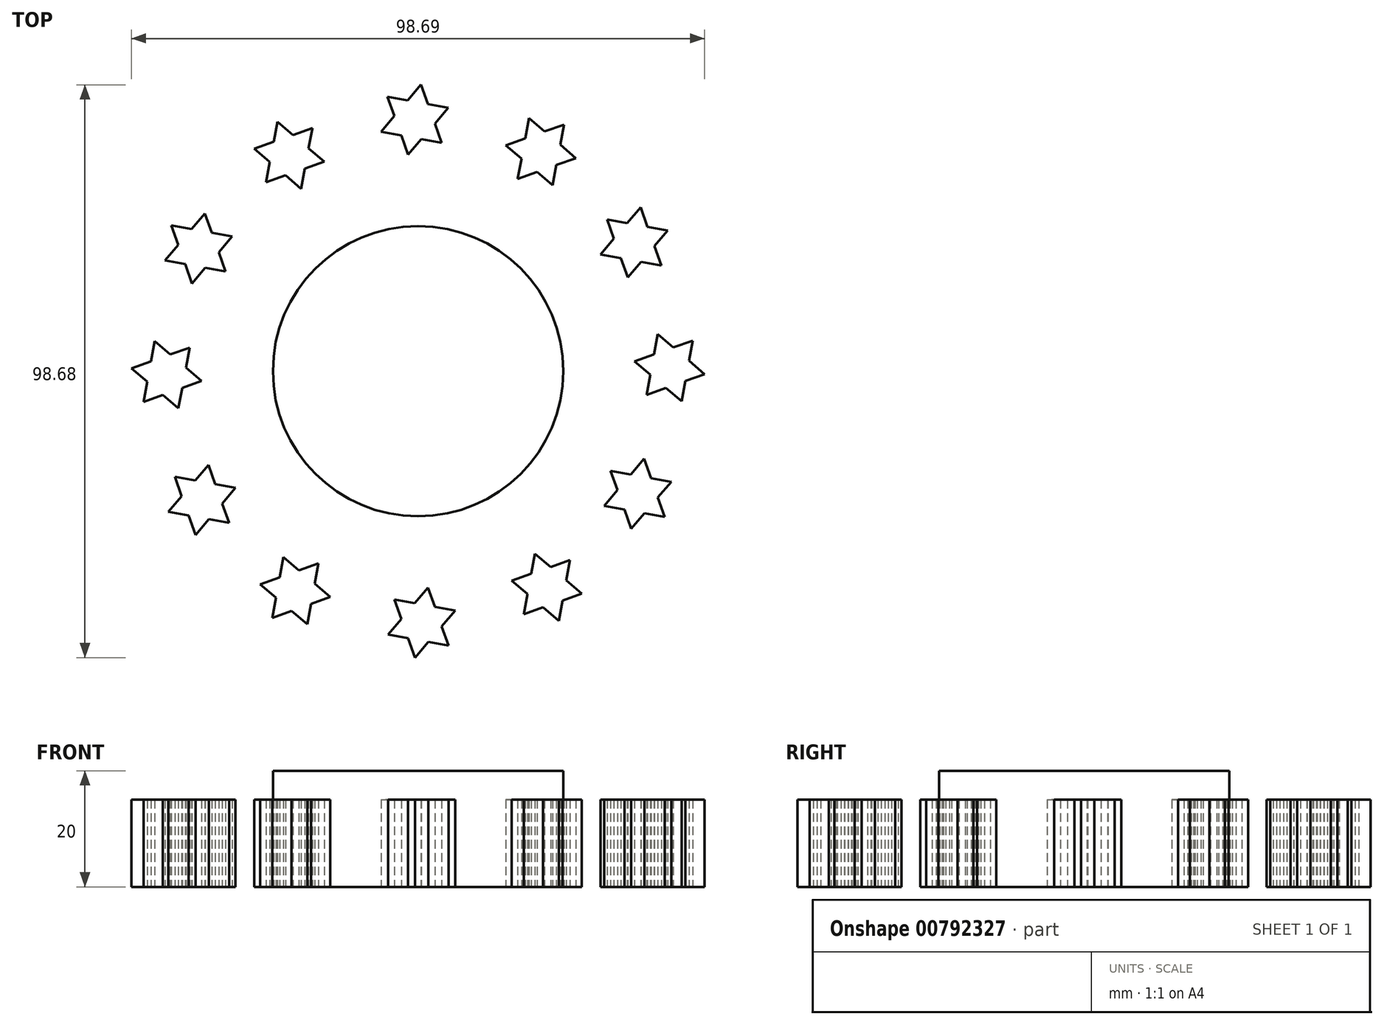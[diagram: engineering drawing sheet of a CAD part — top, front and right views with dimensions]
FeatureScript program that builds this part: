
annotation { "Feature Type Name" : "Feature", "Feature Type Description" : "" }
export const myFeature = defineFeature(function(context is Context, id is Id, definition is map)
    precondition{}
    {
        {
            var Q0;
            Q0=qCreatedBy(makeId("Top.planeOp"),FACE);
            var sketch = newSketch(context, id + "F0", { "sketchPlane" : qUnion([Q0])});
            skCircle(sketch, "E0", {"center": v(0.6, 0) * mm, "radius": 25 * mm});
            skLineSegment(sketch, "E1.0", {"start": v(-1.1, 37.28) * mm, "end": v(-5.78, 41.26) * mm});
            skLineSegment(sketch, "E1.1", {"start": v(-5.78, 41.26) * mm, "end": v(-4.67, 47.29) * mm});
            skLineSegment(sketch, "E1.2", {"start": v(-4.67, 47.29) * mm, "end": v(1.1, 49.34) * mm});
            skLineSegment(sketch, "E1.3", {"start": v(1.1, 49.34) * mm, "end": v(5.78, 45.37) * mm});
            skLineSegment(sketch, "E1.4", {"start": v(5.78, 45.37) * mm, "end": v(4.67, 39.34) * mm});
            skLineSegment(sketch, "E1.5", {"start": v(4.67, 39.34) * mm, "end": v(-1.1, 37.28) * mm});
            skPoint(sketch, "E1.0.midPoint", {"position": v(-3.44, 39.27) * mm});
            skLineSegment(sketch, "E2", {"start": v(-4.67, 47.29) * mm, "end": v(-1.1, 37.28) * mm});
            skLineSegment(sketch, "E3", {"start": v(-4.67, 47.29) * mm, "end": v(5.78, 45.37) * mm});
            skLineSegment(sketch, "E4", {"start": v(-5.78, 41.26) * mm, "end": v(4.67, 39.34) * mm});
            skLineSegment(sketch, "E5", {"start": v(1.1, 49.34) * mm, "end": v(4.67, 39.34) * mm});
            skLineSegment(sketch, "E6", {"start": v(1.1, 49.34) * mm, "end": v(-5.78, 41.26) * mm});
            skLineSegment(sketch, "E7", {"start": v(-1.1, 37.28) * mm, "end": v(5.78, 45.37) * mm});
            skPoint(sketch, "E8.center.orphan", {"position": v(0, 43.31) * mm});
            skSolve(sketch);
        }
        {
            var Q0;
            Q0=makeQuery(id+"F0.imprint","IMPRINT",FACE,{"disambiguationData":[TD([[makeQuery(id+"F0.imprint","IMPRINT",EDGE,{"derivedFrom":sQuery(id+"F0.wireOp",EDGE,"E0")}),1.0]])]});
            extrude(context, id + "F1", {"entities" : qUnion([Q0]), "depth" : 20 * mm, "offsetDistance" : 25 * mm});
        }
        {
            var Q0;
            {var subQ1=sQuery(id+"F0.wireOp",EDGE,"E4");var subQ3=sQuery(id+"F0.wireOp",EDGE,"E7");var subQ4=makeQuery(id+"F0.imprint","INTERSECT",VERTEX,{"derivedFrom":[subQ1,subQ3]});Q0=makeQuery(id+"F0.imprint","IMPRINT",FACE,{"disambiguationData":[TD([[makeQuery(id+"F0.imprint","IMPRINT",EDGE,{"disambiguationData":[TD([[subQ4,-1.0]])],"derivedFrom":subQ3}),-1.0]])]});}
            var Q1;
            {var subQ0=sQuery(id+"F0.wireOp",EDGE,"E6");var subQ1=sQuery(id+"F0.wireOp",EDGE,"E2");var subQ2=makeQuery(id+"F0.imprint","INTERSECT",VERTEX,{"derivedFrom":[subQ1,subQ0]});Q1=makeQuery(id+"F0.imprint","IMPRINT",FACE,{"disambiguationData":[TD([[makeQuery(id+"F0.imprint","IMPRINT",EDGE,{"disambiguationData":[TD([[subQ2,-1.0]])],"derivedFrom":subQ1}),-1.0]])]});}
            var Q2;
            {var subQ1=sQuery(id+"F0.wireOp",EDGE,"E2");var subQ3=sQuery(id+"F0.wireOp",EDGE,"E4");var subQ4=makeQuery(id+"F0.imprint","INTERSECT",VERTEX,{"derivedFrom":[subQ1,subQ3]});Q2=makeQuery(id+"F0.imprint","IMPRINT",FACE,{"disambiguationData":[TD([[makeQuery(id+"F0.imprint","IMPRINT",EDGE,{"disambiguationData":[TD([[subQ4,-1.0]])],"derivedFrom":subQ3}),-1.0]])]});}
            var Q3;
            {var subQ1=sQuery(id+"F0.wireOp",EDGE,"E3");var subQ3=sQuery(id+"F0.wireOp",EDGE,"E5");var subQ4=makeQuery(id+"F0.imprint","INTERSECT",VERTEX,{"derivedFrom":[subQ1,subQ3]});Q3=makeQuery(id+"F0.imprint","IMPRINT",FACE,{"disambiguationData":[TD([[makeQuery(id+"F0.imprint","IMPRINT",EDGE,{"disambiguationData":[TD([[subQ4,-1.0]])],"derivedFrom":subQ3}),1.0]])]});}
            var Q4;
            {var subQ0=sQuery(id+"F0.wireOp",EDGE,"E6");var subQ1=sQuery(id+"F0.wireOp",EDGE,"E3");var subQ2=makeQuery(id+"F0.imprint","INTERSECT",VERTEX,{"derivedFrom":[subQ1,subQ0]});Q4=makeQuery(id+"F0.imprint","IMPRINT",FACE,{"disambiguationData":[TD([[makeQuery(id+"F0.imprint","IMPRINT",EDGE,{"disambiguationData":[TD([[subQ2,-1.0]])],"derivedFrom":subQ1}),1.0]])]});}
            var Q5;
            {var subQ1=sQuery(id+"F0.wireOp",EDGE,"E2");var subQ3=sQuery(id+"F0.wireOp",EDGE,"E6");var subQ4=makeQuery(id+"F0.imprint","INTERSECT",VERTEX,{"derivedFrom":[subQ1,subQ3]});Q5=makeQuery(id+"F0.imprint","IMPRINT",FACE,{"disambiguationData":[TD([[makeQuery(id+"F0.imprint","IMPRINT",EDGE,{"disambiguationData":[TD([[subQ4,1.0]])],"derivedFrom":subQ3}),-1.0]])]});}
            var Q6;
            {var subQ6=sQuery(id+"F0.wireOp",EDGE,"E2");var subQ9=sQuery(id+"F0.wireOp",EDGE,"E6");var subQ11=makeQuery(id+"F0.imprint","INTERSECT",VERTEX,{"derivedFrom":[subQ6,subQ9]});Q6=makeQuery(id+"F0.imprint","IMPRINT",FACE,{"disambiguationData":[TD([[makeQuery(id+"F0.imprint","IMPRINT",EDGE,{"disambiguationData":[TD([[subQ11,-1.0]])],"derivedFrom":subQ6}),1.0]])]});}
            extrude(context, id + "F2", {"entities" : qUnion([Q0, Q1, Q2, Q3, Q4, Q5, Q6]), "depth" : 15 * mm, "offsetDistance" : 25 * mm});
        }
        {
            var Q0;
            Q0=makeQuery(id+"F2.opExtrude","SWEPT_BODY",BODY,{"disambiguationData":[OSD([sQuery(id+"F0.wireOp",EDGE,"E2"),sQuery(id+"F0.wireOp",EDGE,"E3"),sQuery(id+"F0.wireOp",EDGE,"E4"),sQuery(id+"F0.wireOp",EDGE,"E5"),sQuery(id+"F0.wireOp",EDGE,"E6"),sQuery(id+"F0.wireOp",EDGE,"E7")])]});
            var Q1;
            Q1=makeQuery(id+"F1.opExtrude","CAP_EDGE",EDGE,{"disambiguationData":[OSD([sQuery(id+"F0.wireOp",EDGE,"E0")])],"isStart":false});
            circularPattern(context, id + "F3", {"entities" : qUnion([Q0]), "axis" : qUnion([Q1]), "angle" : 360 * degree, "instanceCount" : 12, "equalSpace" : true});
        }
    });
